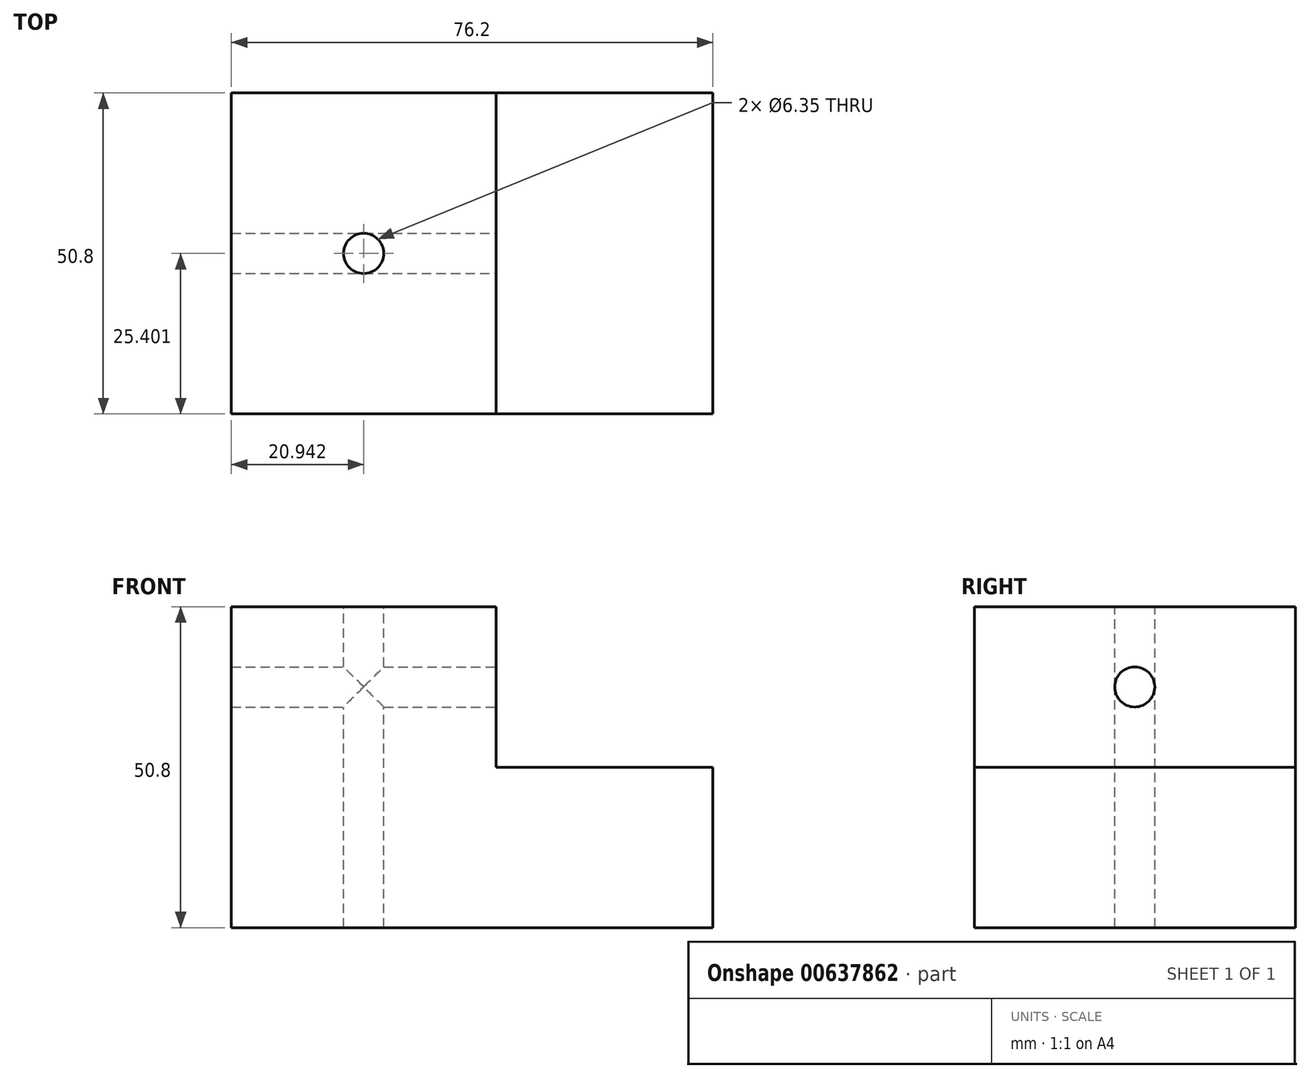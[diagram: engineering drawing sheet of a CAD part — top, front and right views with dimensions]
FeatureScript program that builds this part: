
annotation { "Feature Type Name" : "Feature", "Feature Type Description" : "" }
export const myFeature = defineFeature(function(context is Context, id is Id, definition is map)
    precondition{}
    {
        {
            var Q0;
            Q0=qCreatedBy(makeId("Top.planeOp"),FACE);
            var sketch = newSketch(context, id + "F0", { "sketchPlane" : qUnion([Q0])});
            skLineSegment(sketch, "E0.bottom", {"start": v(-41.88, 40.35) * mm, "end": v(34.32, 40.35) * mm});
            skLineSegment(sketch, "E0.top", {"start": v(-41.88, -10.45) * mm, "end": v(34.32, -10.45) * mm});
            skLineSegment(sketch, "E0.left", {"start": v(-41.88, 40.35) * mm, "end": v(-41.88, -10.45) * mm});
            skLineSegment(sketch, "E0.right", {"start": v(34.32, 40.35) * mm, "end": v(34.32, -10.45) * mm});
            skSolve(sketch);
        }
        {
            var Q0;
            Q0 = qSketchRegion(id + "F0", true);
            extrude(context, id + "F1", {"entities" : qUnion([Q0]), "depth" : 25.4 * mm, "offsetDistance" : 25.4 * mm});
        }
        {
            var Q0;
            Q0=makeQuery(id+"F1.opExtrude","CAP_FACE",FACE,{"disambiguationData":[OSD([sQuery(id+"F0.wireOp",EDGE,"E0.bottom"),sQuery(id+"F0.wireOp",EDGE,"E0.top"),sQuery(id+"F0.wireOp",EDGE,"E0.left"),sQuery(id+"F0.wireOp",EDGE,"E0.right")])],"isStart":false});
            var sketch = newSketch(context, id + "F2", { "sketchPlane" : qUnion([Q0])});
            skLineSegment(sketch, "E1.bottom", {"start": v(-41.88, 40.35) * mm, "end": v(0, 40.35) * mm});
            skLineSegment(sketch, "E1.top", {"start": v(-41.88, -10.45) * mm, "end": v(0, -10.45) * mm});
            skLineSegment(sketch, "E1.left", {"start": v(-41.88, 40.35) * mm, "end": v(-41.88, -10.45) * mm});
            skLineSegment(sketch, "E1.right", {"start": v(0, 40.35) * mm, "end": v(0, -10.45) * mm});
            skSolve(sketch);
        }
        {
            var Q0;
            Q0 = qSketchRegion(id + "F2", true);
            extrude(context, id + "F3", {"entities" : qUnion([Q0]), "operationType" : NewBodyOperationType.ADD, "depth" : 25.4 * mm, "offsetDistance" : 25.4 * mm});
        }
        {
            var Q0;
            Q0=makeQuery(id+"F3.opExtrude","SWEPT_FACE",FACE,{"disambiguationData":[OSD([sQuery(id+"F2.wireOp",EDGE,"E1.right")])]});
            var sketch = newSketch(context, id + "F4", { "sketchPlane" : qUnion([Q0])});
            skPoint(sketch, "E2", {"position": v(14.95, 38.1) * mm});
            skPoint(sketch, "E2.positionSnap0", {"position": v(-10.45, 38.1) * mm});
            skPoint(sketch, "E2.positionSnap1", {"position": v(14.95, 50.8) * mm});
            skSolve(sketch);
        }
        {
            var Q0;
            Q0=sQuery(id+"F4.wireOp",VERTEX,"E2");
            var Q1;
            Q1=makeQuery(id+"F1.opExtrude","SWEPT_BODY",BODY,{"disambiguationData":[OSD([sQuery(id+"F0.wireOp",EDGE,"E0.bottom"),sQuery(id+"F0.wireOp",EDGE,"E0.top"),sQuery(id+"F0.wireOp",EDGE,"E0.left"),sQuery(id+"F0.wireOp",EDGE,"E0.right")])]});
            hole(context, id + "F5", {"style" : HoleStyle.SIMPLE, "endStyle" : HoleEndStyle.THROUGH, "holeDiameter" : 6.35 * mm, "majorDiameter" : 6.35 * mm, "isTappedThrough" : true, "tappedDepth" : 12.7 * mm, "tapClearance" : 3, "locations" : qUnion([Q0]), "scope" : qUnion([Q1])});
        }
        {
            var Q0;
            Q0=makeQuery(id+"F3.opExtrude","CAP_FACE",FACE,{"disambiguationData":[OSD([sQuery(id+"F2.wireOp",EDGE,"E1.bottom"),sQuery(id+"F2.wireOp",EDGE,"E1.top"),sQuery(id+"F2.wireOp",EDGE,"E1.left"),sQuery(id+"F2.wireOp",EDGE,"E1.right")])],"isStart":false});
            var sketch = newSketch(context, id + "F6", { "sketchPlane" : qUnion([Q0])});
            skPoint(sketch, "E3", {"position": v(-20.94, 14.95) * mm});
            skPoint(sketch, "E3.positionSnap0", {"position": v(-20.94, -10.45) * mm});
            skPoint(sketch, "E3.positionSnap1", {"position": v(0, 14.95) * mm});
            skSolve(sketch);
        }
        {
            var Q0;
            Q0=sQuery(id+"F6.wireOp",VERTEX,"E3");
            var Q1;
            Q1=makeQuery(id+"F1.opExtrude","SWEPT_BODY",BODY,{"disambiguationData":[OSD([sQuery(id+"F0.wireOp",EDGE,"E0.bottom"),sQuery(id+"F0.wireOp",EDGE,"E0.top"),sQuery(id+"F0.wireOp",EDGE,"E0.left"),sQuery(id+"F0.wireOp",EDGE,"E0.right")])]});
            hole(context, id + "F7", {"style" : HoleStyle.SIMPLE, "endStyle" : HoleEndStyle.THROUGH, "holeDiameter" : 6.35 * mm, "majorDiameter" : 6.35 * mm, "isTappedThrough" : true, "tappedDepth" : 12.7 * mm, "tapClearance" : 3, "locations" : qUnion([Q0]), "scope" : qUnion([Q1])});
        }
    });
